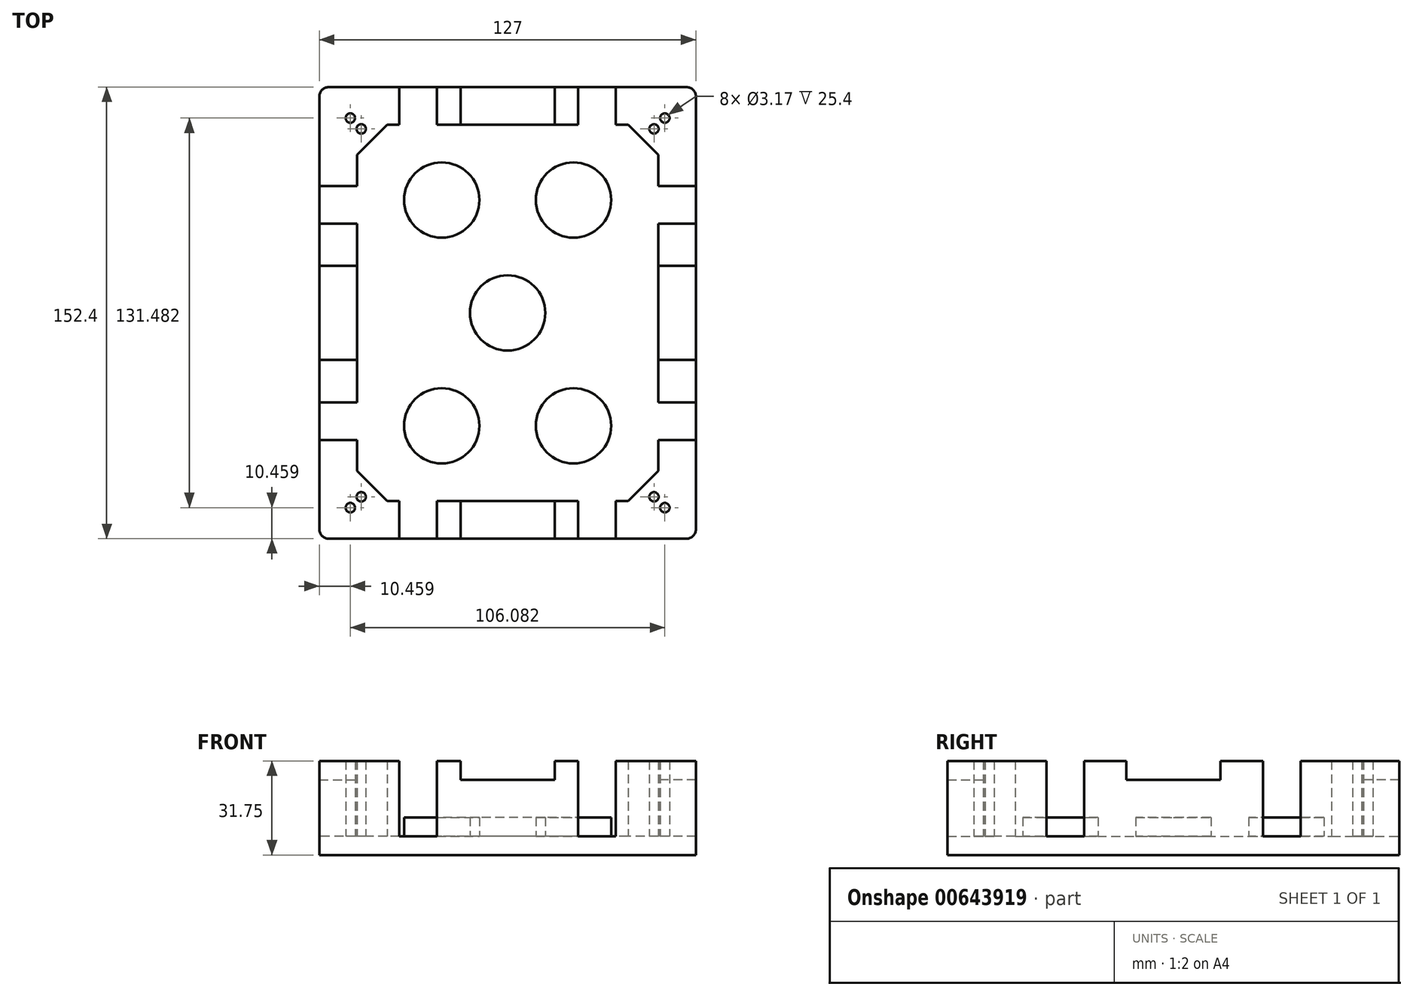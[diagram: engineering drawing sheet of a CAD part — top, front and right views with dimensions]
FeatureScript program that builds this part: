
annotation { "Feature Type Name" : "Feature", "Feature Type Description" : "" }
export const myFeature = defineFeature(function(context is Context, id is Id, definition is map)
    precondition{}
    {
        {
            var Q0;
            Q0=qCreatedBy(makeId("Top.planeOp"),FACE);
            var sketch = newSketch(context, id + "F0", { "sketchPlane" : qUnion([Q0])});
            skLineSegment(sketch, "E0.bottom", {"start": v(-60.32, 76.2) * mm, "end": v(60.33, 76.2) * mm});
            skLineSegment(sketch, "E0.top", {"start": v(-60.33, -76.2) * mm, "end": v(60.33, -76.2) * mm});
            skLineSegment(sketch, "E0.left", {"start": v(-63.5, 73.03) * mm, "end": v(-63.5, -73.03) * mm});
            skLineSegment(sketch, "E0.right", {"start": v(63.5, 73.03) * mm, "end": v(63.5, -73.03) * mm});
            skPoint(sketch, "E0.middle", {"position": v(0, 0) * mm});
            skLineSegment(sketch, "E1.bottom", {"start": v(-53.98, 69.85) * mm, "end": v(53.98, 69.85) * mm});
            skLineSegment(sketch, "E1.top", {"start": v(-53.98, -69.85) * mm, "end": v(53.97, -69.85) * mm});
            skLineSegment(sketch, "E1.left", {"start": v(-57.15, 66.68) * mm, "end": v(-57.15, -66.68) * mm});
            skLineSegment(sketch, "E1.right", {"start": v(57.15, 66.68) * mm, "end": v(57.15, -66.68) * mm});
            skLineSegment(sketch, "E2.bottom", {"start": v(-47.63, 63.5) * mm, "end": v(47.63, 63.5) * mm});
            skLineSegment(sketch, "E2.top", {"start": v(-47.63, -63.5) * mm, "end": v(48.25, -63.5) * mm});
            skLineSegment(sketch, "E2.left", {"start": v(-50.8, 60.33) * mm, "end": v(-50.8, -60.33) * mm});
            skLineSegment(sketch, "E2.right", {"start": v(50.8, 60.33) * mm, "end": v(50.8, -60.95) * mm});
            skPoint(sketch, "E3.visualSharp", {"position": v(-57.15, 69.85) * mm});
            skArc(sketch, "E3.filletArc", {"start": v(-53.98, 69.85) * mm, "mid": v(-56.22, 68.92) * mm, "end": v(-57.15, 66.68) * mm});
            skPoint(sketch, "E4.visualSharp", {"position": v(57.15, 69.85) * mm});
            skArc(sketch, "E4.filletArc", {"start": v(57.15, 66.68) * mm, "mid": v(56.22, 68.92) * mm, "end": v(53.98, 69.85) * mm});
            skPoint(sketch, "E5.visualSharp", {"position": v(57.15, -69.85) * mm});
            skArc(sketch, "E5.filletArc", {"start": v(53.97, -69.85) * mm, "mid": v(56.22, -68.92) * mm, "end": v(57.15, -66.68) * mm});
            skPoint(sketch, "E6.visualSharp", {"position": v(-57.15, -69.85) * mm});
            skArc(sketch, "E6.filletArc", {"start": v(-57.15, -66.68) * mm, "mid": v(-56.22, -68.92) * mm, "end": v(-53.98, -69.85) * mm});
            skPoint(sketch, "E7.visualSharp", {"position": v(50.8, 63.5) * mm});
            skArc(sketch, "E7.filletArc", {"start": v(50.8, 60.33) * mm, "mid": v(49.87, 62.57) * mm, "end": v(47.63, 63.5) * mm});
            skPoint(sketch, "E8.visualSharp", {"position": v(50.8, -63.5) * mm});
            skArc(sketch, "E8.filletArc", {"start": v(48.25, -63.5) * mm, "mid": v(50.05, -62.75) * mm, "end": v(50.8, -60.95) * mm});
            skPoint(sketch, "E9.visualSharp", {"position": v(-50.8, -63.5) * mm});
            skArc(sketch, "E9.filletArc", {"start": v(-50.8, -60.33) * mm, "mid": v(-49.87, -62.57) * mm, "end": v(-47.63, -63.5) * mm});
            skArc(sketch, "E10.filletArc", {"start": v(-47.63, 63.5) * mm, "mid": v(-49.87, 62.57) * mm, "end": v(-50.8, 60.33) * mm});
            skPoint(sketch, "E11.visualSharp", {"position": v(-63.5, 76.2) * mm});
            skArc(sketch, "E11.filletArc", {"start": v(-60.32, 76.2) * mm, "mid": v(-62.57, 75.27) * mm, "end": v(-63.5, 73.03) * mm});
            skPoint(sketch, "E12.visualSharp", {"position": v(63.5, 76.2) * mm});
            skArc(sketch, "E12.filletArc", {"start": v(63.5, 73.03) * mm, "mid": v(62.57, 75.27) * mm, "end": v(60.33, 76.2) * mm});
            skPoint(sketch, "E13.visualSharp", {"position": v(63.5, -76.2) * mm});
            skArc(sketch, "E13.filletArc", {"start": v(60.33, -76.2) * mm, "mid": v(62.57, -75.27) * mm, "end": v(63.5, -73.03) * mm});
            skPoint(sketch, "E14.visualSharp", {"position": v(-63.5, -76.2) * mm});
            skArc(sketch, "E14.filletArc", {"start": v(-63.5, -73.03) * mm, "mid": v(-62.57, -75.27) * mm, "end": v(-60.33, -76.2) * mm});
            skLineSegment(sketch, "E15.bottom", {"start": v(-34.92, 50.8) * mm, "end": v(34.93, 50.8) * mm});
            skLineSegment(sketch, "E15.top", {"start": v(-34.93, -50.8) * mm, "end": v(34.92, -50.8) * mm});
            skLineSegment(sketch, "E15.left", {"start": v(-34.92, 50.8) * mm, "end": v(-34.93, -50.8) * mm});
            skLineSegment(sketch, "E15.right", {"start": v(34.93, 50.8) * mm, "end": v(34.92, -50.8) * mm});
            skPoint(sketch, "E16", {"position": v(22.23, -50.8) * mm});
            skPoint(sketch, "E17", {"position": v(22.23, 50.8) * mm});
            skPoint(sketch, "E18", {"position": v(-22.22, 50.8) * mm});
            skPoint(sketch, "E19", {"position": v(-22.22, -50.8) * mm});
            skPoint(sketch, "E20", {"position": v(34.93, 38.1) * mm});
            skPoint(sketch, "E21", {"position": v(-34.92, 38.1) * mm});
            skPoint(sketch, "E22", {"position": v(34.92, -38.1) * mm});
            skPoint(sketch, "E23", {"position": v(-34.93, -38.1) * mm});
            skPoint(sketch, "E24", {"position": v(-22.22, 38.1) * mm});
            skPoint(sketch, "E25", {"position": v(22.23, 38.1) * mm});
            skPoint(sketch, "E26", {"position": v(22.23, -38.1) * mm});
            skPoint(sketch, "E27", {"position": v(-22.22, -38.1) * mm});
            skCircle(sketch, "E28", {"center": v(-22.22, 38.1) * mm, "radius": 12.7 * mm});
            skCircle(sketch, "E29", {"center": v(0, 0) * mm, "radius": 12.7 * mm});
            skCircle(sketch, "E30", {"center": v(22.23, 38.1) * mm, "radius": 12.7 * mm});
            skCircle(sketch, "E31", {"center": v(-22.22, -38.1) * mm, "radius": 12.7 * mm});
            skCircle(sketch, "E32", {"center": v(22.23, -38.1) * mm, "radius": 12.7 * mm});
            skPoint(sketch, "E33", {"position": v(15.88, 63.5) * mm});
            skPoint(sketch, "E34", {"position": v(15.88, 76.2) * mm});
            skPoint(sketch, "E35", {"position": v(15.88, -63.5) * mm});
            skPoint(sketch, "E36", {"position": v(15.88, -76.2) * mm});
            skPoint(sketch, "E37", {"position": v(-15.88, 76.2) * mm});
            skPoint(sketch, "E38", {"position": v(-15.88, 63.5) * mm});
            skPoint(sketch, "E39", {"position": v(-15.88, -63.5) * mm});
            skPoint(sketch, "E40", {"position": v(-15.88, -76.2) * mm});
            skPoint(sketch, "E41", {"position": v(0, 76.2) * mm});
            skPoint(sketch, "E42", {"position": v(0, -76.2) * mm});
            skPoint(sketch, "E43", {"position": v(-63.5, 0) * mm});
            skPoint(sketch, "E44", {"position": v(63.5, 0) * mm});
            skPoint(sketch, "E45", {"position": v(63.5, 15.88) * mm});
            skPoint(sketch, "E46", {"position": v(50.8, 15.88) * mm});
            skPoint(sketch, "E47", {"position": v(-50.8, 15.88) * mm});
            skPoint(sketch, "E48", {"position": v(-63.5, 15.88) * mm});
            skPoint(sketch, "E49", {"position": v(63.5, -15.88) * mm});
            skPoint(sketch, "E50", {"position": v(50.8, -15.88) * mm});
            skPoint(sketch, "E51", {"position": v(-50.8, -15.88) * mm});
            skPoint(sketch, "E52", {"position": v(-63.5, -15.88) * mm});
            skLineSegment(sketch, "E53", {"start": v(-15.88, 76.2) * mm, "end": v(-15.88, 63.5) * mm});
            skLineSegment(sketch, "E54", {"start": v(15.88, 76.2) * mm, "end": v(15.88, 63.5) * mm});
            skLineSegment(sketch, "E55", {"start": v(63.5, 15.88) * mm, "end": v(50.8, 15.88) * mm});
            skLineSegment(sketch, "E56", {"start": v(63.5, -15.88) * mm, "end": v(50.8, -15.88) * mm});
            skLineSegment(sketch, "E57", {"start": v(15.88, -76.2) * mm, "end": v(15.88, -63.5) * mm});
            skLineSegment(sketch, "E58", {"start": v(-15.88, -76.2) * mm, "end": v(-15.88, -63.5) * mm});
            skLineSegment(sketch, "E59", {"start": v(-63.5, -15.88) * mm, "end": v(-50.8, -15.88) * mm});
            skLineSegment(sketch, "E60", {"start": v(-63.5, 15.88) * mm, "end": v(-50.8, 15.88) * mm});
            skPoint(sketch, "E61", {"position": v(40.64, 63.5) * mm});
            skPoint(sketch, "E62", {"position": v(40.64, -63.5) * mm});
            skPoint(sketch, "E63", {"position": v(-40.64, 63.5) * mm});
            skPoint(sketch, "E64", {"position": v(-40.64, -63.5) * mm});
            skPoint(sketch, "E65", {"position": v(-50.8, -53.34) * mm});
            skPoint(sketch, "E66", {"position": v(50.8, -53.34) * mm});
            skPoint(sketch, "E67", {"position": v(50.8, 53.34) * mm});
            skPoint(sketch, "E68", {"position": v(-50.8, 53.34) * mm});
            skLineSegment(sketch, "E69", {"start": v(-50.8, 53.34) * mm, "end": v(-40.64, 63.5) * mm});
            skLineSegment(sketch, "E70", {"start": v(40.64, 63.5) * mm, "end": v(50.8, 53.34) * mm});
            skLineSegment(sketch, "E71", {"start": v(50.8, -53.34) * mm, "end": v(40.64, -63.5) * mm});
            skLineSegment(sketch, "E72", {"start": v(-40.64, -63.5) * mm, "end": v(-50.8, -53.34) * mm});
            skPoint(sketch, "E73", {"position": v(-45.72, 58.42) * mm});
            skPoint(sketch, "E74", {"position": v(45.72, 58.42) * mm});
            skPoint(sketch, "E75", {"position": v(45.72, -58.42) * mm});
            skPoint(sketch, "E76", {"position": v(-45.72, -58.42) * mm});
            skPoint(sketch, "E77", {"position": v(30.16, 76.2) * mm});
            skPoint(sketch, "E78", {"position": v(30.16, 63.5) * mm});
            skPoint(sketch, "E79", {"position": v(30.16, -63.5) * mm});
            skPoint(sketch, "E80", {"position": v(30.16, -76.2) * mm});
            skPoint(sketch, "E81", {"position": v(-30.16, 76.2) * mm});
            skPoint(sketch, "E82", {"position": v(-30.16, 63.5) * mm});
            skPoint(sketch, "E83", {"position": v(-30.16, -63.5) * mm});
            skPoint(sketch, "E84", {"position": v(-30.16, -76.2) * mm});
            skPoint(sketch, "E85", {"position": v(63.5, 36.51) * mm});
            skPoint(sketch, "E86", {"position": v(50.8, 36.51) * mm});
            skPoint(sketch, "E87", {"position": v(-50.8, 36.51) * mm});
            skPoint(sketch, "E88", {"position": v(-63.5, 36.51) * mm});
            skPoint(sketch, "E89", {"position": v(63.5, -36.51) * mm});
            skPoint(sketch, "E90", {"position": v(50.8, -36.51) * mm});
            skPoint(sketch, "E91", {"position": v(-50.8, -36.51) * mm});
            skPoint(sketch, "E92", {"position": v(-63.5, -36.51) * mm});
            skPoint(sketch, "E93", {"position": v(-36.51, 76.2) * mm});
            skPoint(sketch, "E94", {"position": v(-36.51, 63.5) * mm});
            skPoint(sketch, "E95", {"position": v(-36.51, -63.5) * mm});
            skPoint(sketch, "E96", {"position": v(-36.51, -76.2) * mm});
            skPoint(sketch, "E97", {"position": v(36.51, 76.2) * mm});
            skPoint(sketch, "E98", {"position": v(36.51, 63.5) * mm});
            skPoint(sketch, "E99", {"position": v(36.51, -63.5) * mm});
            skPoint(sketch, "E100", {"position": v(36.51, -76.2) * mm});
            skPoint(sketch, "E101", {"position": v(-23.81, 76.2) * mm});
            skPoint(sketch, "E102", {"position": v(-23.81, 63.5) * mm});
            skPoint(sketch, "E103", {"position": v(23.81, 76.2) * mm});
            skPoint(sketch, "E104", {"position": v(23.81, 63.5) * mm});
            skPoint(sketch, "E105", {"position": v(23.81, -63.5) * mm});
            skPoint(sketch, "E106", {"position": v(23.81, -76.2) * mm});
            skPoint(sketch, "E107", {"position": v(-23.81, -63.5) * mm});
            skPoint(sketch, "E108", {"position": v(-23.81, -76.2) * mm});
            skLineSegment(sketch, "E109", {"start": v(-36.51, 76.2) * mm, "end": v(-36.51, 63.5) * mm});
            skLineSegment(sketch, "E110", {"start": v(-23.81, 76.2) * mm, "end": v(-23.81, 63.5) * mm});
            skLineSegment(sketch, "E111", {"start": v(23.81, 76.2) * mm, "end": v(23.81, 63.5) * mm});
            skLineSegment(sketch, "E112", {"start": v(36.51, 76.2) * mm, "end": v(36.51, 63.5) * mm});
            skLineSegment(sketch, "E113", {"start": v(36.51, -63.5) * mm, "end": v(36.51, -76.2) * mm});
            skLineSegment(sketch, "E114", {"start": v(23.81, -63.5) * mm, "end": v(23.81, -76.2) * mm});
            skLineSegment(sketch, "E115", {"start": v(-23.81, -63.5) * mm, "end": v(-23.81, -76.2) * mm});
            skLineSegment(sketch, "E116", {"start": v(-36.51, -63.5) * mm, "end": v(-36.51, -76.2) * mm});
            skPoint(sketch, "E117", {"position": v(-63.5, 42.86) * mm});
            skPoint(sketch, "E118", {"position": v(-50.8, 42.86) * mm});
            skPoint(sketch, "E119", {"position": v(50.8, 42.86) * mm});
            skPoint(sketch, "E120", {"position": v(63.5, 42.86) * mm});
            skPoint(sketch, "E121", {"position": v(-63.5, 30.16) * mm});
            skPoint(sketch, "E122", {"position": v(-50.8, 30.16) * mm});
            skPoint(sketch, "E123", {"position": v(50.8, 30.16) * mm});
            skPoint(sketch, "E124", {"position": v(63.5, 30.16) * mm});
            skPoint(sketch, "E125", {"position": v(-63.5, -30.16) * mm});
            skPoint(sketch, "E126", {"position": v(-50.8, -30.16) * mm});
            skPoint(sketch, "E127", {"position": v(50.8, -30.16) * mm});
            skPoint(sketch, "E128", {"position": v(63.5, -30.16) * mm});
            skPoint(sketch, "E129", {"position": v(-63.5, -42.86) * mm});
            skPoint(sketch, "E130", {"position": v(-50.8, -42.86) * mm});
            skPoint(sketch, "E131", {"position": v(50.8, -42.86) * mm});
            skPoint(sketch, "E132", {"position": v(63.5, -42.86) * mm});
            skLineSegment(sketch, "E133", {"start": v(-63.5, 42.86) * mm, "end": v(-50.8, 42.86) * mm});
            skLineSegment(sketch, "E134", {"start": v(-63.5, 30.16) * mm, "end": v(-50.8, 30.16) * mm});
            skLineSegment(sketch, "E135", {"start": v(50.8, 42.86) * mm, "end": v(63.5, 42.86) * mm});
            skLineSegment(sketch, "E136", {"start": v(50.8, 30.16) * mm, "end": v(63.5, 30.16) * mm});
            skLineSegment(sketch, "E137", {"start": v(50.8, -30.16) * mm, "end": v(63.5, -30.16) * mm});
            skLineSegment(sketch, "E138", {"start": v(50.8, -42.86) * mm, "end": v(63.5, -42.86) * mm});
            skLineSegment(sketch, "E139", {"start": v(-50.8, -42.86) * mm, "end": v(-63.5, -42.86) * mm});
            skLineSegment(sketch, "E140", {"start": v(-50.8, -30.16) * mm, "end": v(-63.5, -30.16) * mm});
            skLineSegment(sketch, "E141", {"start": v(57.15, 69.85) * mm, "end": v(45.72, 58.42) * mm, "construction": true});
            skLineSegment(sketch, "E142", {"start": v(57.15, -69.85) * mm, "end": v(45.72, -58.42) * mm, "construction": true});
            skLineSegment(sketch, "E143", {"start": v(-57.15, -69.85) * mm, "end": v(-45.72, -58.42) * mm, "construction": true});
            skPoint(sketch, "E144", {"position": v(53.04, 65.74) * mm});
            skLineSegment(sketch, "E145", {"start": v(-57.15, 69.85) * mm, "end": v(-45.72, 58.42) * mm, "construction": true});
            skPoint(sketch, "E146", {"position": v(-53.04, 65.74) * mm});
            skPoint(sketch, "E147", {"position": v(53.04, -65.74) * mm});
            skPoint(sketch, "E148", {"position": v(-53.04, -65.74) * mm});
            skCircle(sketch, "E149", {"center": v(-53.04, 65.74) * mm, "radius": 1.59 * mm});
            skCircle(sketch, "E150", {"center": v(53.04, 65.74) * mm, "radius": 1.59 * mm});
            skCircle(sketch, "E151", {"center": v(53.04, -65.74) * mm, "radius": 1.59 * mm});
            skCircle(sketch, "E152", {"center": v(-53.04, -65.74) * mm, "radius": 1.59 * mm});
            skPoint(sketch, "E153", {"position": v(-49.38, -62.08) * mm});
            skPoint(sketch, "E154", {"position": v(49.38, -62.08) * mm});
            skCircle(sketch, "E155", {"center": v(-49.38, -62.08) * mm, "radius": 1.59 * mm});
            skCircle(sketch, "E156", {"center": v(49.38, -62.08) * mm, "radius": 1.59 * mm});
            skPoint(sketch, "E157", {"position": v(-49.38, 62.08) * mm});
            skPoint(sketch, "E158", {"position": v(49.38, 62.08) * mm});
            skCircle(sketch, "E159", {"center": v(-49.38, 62.08) * mm, "radius": 1.59 * mm});
            skCircle(sketch, "E160", {"center": v(49.38, 62.08) * mm, "radius": 1.59 * mm});
            skSolve(sketch);
        }
        {
            var Q0;
            {var subQ0=sQuery(id+"F0.wireOp",EDGE,"E30");var subQ1=makeQuery(id+"F0.imprint","INTERSECT",VERTEX,{"derivedFrom":[sQuery(id+"F0.wireOp",EDGE,"E15.bottom"),subQ0]});Q0=makeQuery(id+"F0.imprint","IMPRINT",FACE,{"disambiguationData":[TD([[makeQuery(id+"F0.imprint","IMPRINT",EDGE,{"disambiguationData":[TD([[subQ1,1.0]])],"derivedFrom":subQ0}),1.0]])]});}
            var Q1;
            {var subQ0=sQuery(id+"F0.wireOp",EDGE,"E15.right");var subQ1=sQuery(id+"F0.wireOp",EDGE,"E15.bottom");var subQ2=makeQuery(id+"F0.imprint","INTERSECT",VERTEX,{"derivedFrom":[subQ1,subQ0]});Q1=makeQuery(id+"F0.imprint","IMPRINT",FACE,{"disambiguationData":[TD([[makeQuery(id+"F0.imprint","IMPRINT",EDGE,{"disambiguationData":[TD([[subQ2,1.0]])],"derivedFrom":subQ1}),-1.0]])]});}
            var Q2;
            {var subQ5=sQuery(id+"F0.wireOp",EDGE,"E6.filletArc");Q2=makeQuery(id+"F0.imprint","IMPRINT",FACE,{"disambiguationData":[TD([[makeQuery(id+"F0.imprint","IMPRINT",EDGE,{"derivedFrom":subQ5}),1.0]])]});}
            var Q3;
            {var subQ0=sQuery(id+"F0.wireOp",EDGE,"E15.right");var subQ1=sQuery(id+"F0.wireOp",EDGE,"E15.top");var subQ2=makeQuery(id+"F0.imprint","INTERSECT",VERTEX,{"derivedFrom":[subQ1,subQ0]});Q3=makeQuery(id+"F0.imprint","IMPRINT",FACE,{"disambiguationData":[TD([[makeQuery(id+"F0.imprint","IMPRINT",EDGE,{"disambiguationData":[TD([[subQ2,1.0]])],"derivedFrom":subQ1}),1.0]])]});}
            var Q4;
            Q4=makeQuery(id+"F0.imprint","IMPRINT",FACE,{"disambiguationData":[TD([[makeQuery(id+"F0.imprint","IMPRINT",EDGE,{"derivedFrom":sQuery(id+"F0.wireOp",EDGE,"E29")}),-1.0]])]});
            var Q5;
            {var subQ0=sQuery(id+"F0.wireOp",EDGE,"E10.filletArc");Q5=makeQuery(id+"F0.imprint","IMPRINT",FACE,{"disambiguationData":[TD([[makeQuery(id+"F0.imprint","IMPRINT",EDGE,{"derivedFrom":subQ0}),1.0]])]});}
            var Q6;
            {var subQ0=sQuery(id+"F0.wireOp",EDGE,"E139");var subQ1=sQuery(id+"F0.wireOp",EDGE,"E0.left");var subQ2=makeQuery(id+"F0.imprint","INTERSECT",VERTEX,{"derivedFrom":[subQ1,subQ0]});Q6=makeQuery(id+"F0.imprint","IMPRINT",FACE,{"disambiguationData":[TD([[makeQuery(id+"F0.imprint","IMPRINT",EDGE,{"disambiguationData":[TD([[subQ2,1.0]])],"derivedFrom":subQ1}),1.0]])]});}
            var Q7;
            {var subQ0=sQuery(id+"F0.wireOp",EDGE,"E6.filletArc");Q7=makeQuery(id+"F0.imprint","IMPRINT",FACE,{"disambiguationData":[TD([[makeQuery(id+"F0.imprint","IMPRINT",EDGE,{"derivedFrom":subQ0}),-1.0]])]});}
            var Q8;
            {var subQ0=sQuery(id+"F0.wireOp",EDGE,"E56");var subQ1=sQuery(id+"F0.wireOp",EDGE,"E0.right");var subQ2=makeQuery(id+"F0.imprint","INTERSECT",VERTEX,{"derivedFrom":[subQ1,subQ0]});Q8=makeQuery(id+"F0.imprint","IMPRINT",FACE,{"disambiguationData":[TD([[makeQuery(id+"F0.imprint","IMPRINT",EDGE,{"disambiguationData":[TD([[subQ2,-1.0]])],"derivedFrom":subQ1}),-1.0]])]});}
            var Q9;
            {var subQ0=sQuery(id+"F0.wireOp",EDGE,"E57");var subQ1=sQuery(id+"F0.wireOp",EDGE,"E1.top");var subQ2=makeQuery(id+"F0.imprint","INTERSECT",VERTEX,{"derivedFrom":[subQ1,subQ0]});Q9=makeQuery(id+"F0.imprint","IMPRINT",FACE,{"disambiguationData":[TD([[makeQuery(id+"F0.imprint","IMPRINT",EDGE,{"disambiguationData":[TD([[subQ2,-1.0]])],"derivedFrom":subQ1}),1.0]])]});}
            var Q10;
            {var subQ0=sQuery(id+"F0.wireOp",EDGE,"E59");var subQ1=sQuery(id+"F0.wireOp",EDGE,"E0.left");var subQ2=makeQuery(id+"F0.imprint","INTERSECT",VERTEX,{"derivedFrom":[subQ1,subQ0]});Q10=makeQuery(id+"F0.imprint","IMPRINT",FACE,{"disambiguationData":[TD([[makeQuery(id+"F0.imprint","IMPRINT",EDGE,{"disambiguationData":[TD([[subQ2,1.0]])],"derivedFrom":subQ1}),1.0]])]});}
            var Q11;
            {var subQ0=sQuery(id+"F0.wireOp",EDGE,"E135");var subQ1=sQuery(id+"F0.wireOp",EDGE,"E1.right");var subQ2=makeQuery(id+"F0.imprint","INTERSECT",VERTEX,{"derivedFrom":[subQ1,subQ0]});Q11=makeQuery(id+"F0.imprint","IMPRINT",FACE,{"disambiguationData":[TD([[makeQuery(id+"F0.imprint","IMPRINT",EDGE,{"disambiguationData":[TD([[subQ2,-1.0]])],"derivedFrom":subQ1}),-1.0]])]});}
            var Q12;
            {var subQ0=sQuery(id+"F0.wireOp",EDGE,"E111");var subQ1=sQuery(id+"F0.wireOp",EDGE,"E0.bottom");var subQ2=makeQuery(id+"F0.imprint","INTERSECT",VERTEX,{"derivedFrom":[subQ1,subQ0]});Q12=makeQuery(id+"F0.imprint","IMPRINT",FACE,{"disambiguationData":[TD([[makeQuery(id+"F0.imprint","IMPRINT",EDGE,{"disambiguationData":[TD([[subQ2,-1.0]])],"derivedFrom":subQ1}),-1.0]])]});}
            var Q13;
            Q13=makeQuery(id+"F0.imprint","IMPRINT",FACE,{"disambiguationData":[TD([[makeQuery(id+"F0.imprint","IMPRINT",EDGE,{"derivedFrom":sQuery(id+"F0.wireOp",EDGE,"E29")}),1.0]])]});
            var Q14;
            {var subQ0=sQuery(id+"F0.wireOp",EDGE,"E137");var subQ1=sQuery(id+"F0.wireOp",EDGE,"E0.right");var subQ2=makeQuery(id+"F0.imprint","INTERSECT",VERTEX,{"derivedFrom":[subQ1,subQ0]});Q14=makeQuery(id+"F0.imprint","IMPRINT",FACE,{"disambiguationData":[TD([[makeQuery(id+"F0.imprint","IMPRINT",EDGE,{"disambiguationData":[TD([[subQ2,-1.0]])],"derivedFrom":subQ1}),-1.0]])]});}
            var Q15;
            {var subQ0=sQuery(id+"F0.wireOp",EDGE,"E31");var subQ1=makeQuery(id+"F0.imprint","INTERSECT",VERTEX,{"derivedFrom":[sQuery(id+"F0.wireOp",EDGE,"E15.top"),subQ0]});Q15=makeQuery(id+"F0.imprint","IMPRINT",FACE,{"disambiguationData":[TD([[makeQuery(id+"F0.imprint","IMPRINT",EDGE,{"disambiguationData":[TD([[subQ1,1.0]])],"derivedFrom":subQ0}),1.0]])]});}
            var Q16;
            {var subQ0=sQuery(id+"F0.wireOp",EDGE,"E59");var subQ1=sQuery(id+"F0.wireOp",EDGE,"E1.left");var subQ2=makeQuery(id+"F0.imprint","INTERSECT",VERTEX,{"derivedFrom":[subQ1,subQ0]});Q16=makeQuery(id+"F0.imprint","IMPRINT",FACE,{"disambiguationData":[TD([[makeQuery(id+"F0.imprint","IMPRINT",EDGE,{"disambiguationData":[TD([[subQ2,-1.0]])],"derivedFrom":subQ1}),1.0]])]});}
            var Q17;
            {var subQ0=sQuery(id+"F0.wireOp",EDGE,"E9.filletArc");Q17=makeQuery(id+"F0.imprint","IMPRINT",FACE,{"disambiguationData":[TD([[makeQuery(id+"F0.imprint","IMPRINT",EDGE,{"derivedFrom":subQ0}),1.0]])]});}
            var Q18;
            {var subQ0=sQuery(id+"F0.wireOp",EDGE,"E32");var subQ1=makeQuery(id+"F0.imprint","INTERSECT",VERTEX,{"derivedFrom":[sQuery(id+"F0.wireOp",EDGE,"E15.top"),subQ0]});Q18=makeQuery(id+"F0.imprint","IMPRINT",FACE,{"disambiguationData":[TD([[makeQuery(id+"F0.imprint","IMPRINT",EDGE,{"disambiguationData":[TD([[subQ1,1.0]])],"derivedFrom":subQ0}),1.0]])]});}
            var Q19;
            {var subQ0=sQuery(id+"F0.wireOp",EDGE,"E115");var subQ1=sQuery(id+"F0.wireOp",EDGE,"E1.top");var subQ2=makeQuery(id+"F0.imprint","INTERSECT",VERTEX,{"derivedFrom":[subQ1,subQ0]});Q19=makeQuery(id+"F0.imprint","IMPRINT",FACE,{"disambiguationData":[TD([[makeQuery(id+"F0.imprint","IMPRINT",EDGE,{"disambiguationData":[TD([[subQ2,-1.0]])],"derivedFrom":subQ1}),1.0]])]});}
            var Q20;
            {var subQ0=sQuery(id+"F0.wireOp",EDGE,"E135");var subQ1=sQuery(id+"F0.wireOp",EDGE,"E0.right");var subQ2=makeQuery(id+"F0.imprint","INTERSECT",VERTEX,{"derivedFrom":[subQ1,subQ0]});Q20=makeQuery(id+"F0.imprint","IMPRINT",FACE,{"disambiguationData":[TD([[makeQuery(id+"F0.imprint","IMPRINT",EDGE,{"disambiguationData":[TD([[subQ2,-1.0]])],"derivedFrom":subQ1}),-1.0]])]});}
            var Q21;
            {var subQ0=sQuery(id+"F0.wireOp",EDGE,"E57");var subQ1=sQuery(id+"F0.wireOp",EDGE,"E0.top");var subQ2=makeQuery(id+"F0.imprint","INTERSECT",VERTEX,{"derivedFrom":[subQ1,subQ0]});Q21=makeQuery(id+"F0.imprint","IMPRINT",FACE,{"disambiguationData":[TD([[makeQuery(id+"F0.imprint","IMPRINT",EDGE,{"disambiguationData":[TD([[subQ2,1.0]])],"derivedFrom":subQ1}),1.0]])]});}
            var Q22;
            {var subQ0=sQuery(id+"F0.wireOp",EDGE,"E134");var subQ1=sQuery(id+"F0.wireOp",EDGE,"E1.left");var subQ2=makeQuery(id+"F0.imprint","INTERSECT",VERTEX,{"derivedFrom":[subQ1,subQ0]});Q22=makeQuery(id+"F0.imprint","IMPRINT",FACE,{"disambiguationData":[TD([[makeQuery(id+"F0.imprint","IMPRINT",EDGE,{"disambiguationData":[TD([[subQ2,-1.0]])],"derivedFrom":subQ1}),1.0]])]});}
            var Q23;
            {var subQ8=sQuery(id+"F0.wireOp",EDGE,"E4.filletArc");Q23=makeQuery(id+"F0.imprint","IMPRINT",FACE,{"disambiguationData":[TD([[makeQuery(id+"F0.imprint","IMPRINT",EDGE,{"derivedFrom":subQ8}),1.0]])]});}
            var Q24;
            {var subQ0=sQuery(id+"F0.wireOp",EDGE,"E7.filletArc");Q24=makeQuery(id+"F0.imprint","IMPRINT",FACE,{"disambiguationData":[TD([[makeQuery(id+"F0.imprint","IMPRINT",EDGE,{"derivedFrom":subQ0}),1.0]])]});}
            var Q25;
            {var subQ0=sQuery(id+"F0.wireOp",EDGE,"E133");var subQ1=sQuery(id+"F0.wireOp",EDGE,"E0.left");var subQ2=makeQuery(id+"F0.imprint","INTERSECT",VERTEX,{"derivedFrom":[subQ1,subQ0]});Q25=makeQuery(id+"F0.imprint","IMPRINT",FACE,{"disambiguationData":[TD([[makeQuery(id+"F0.imprint","IMPRINT",EDGE,{"disambiguationData":[TD([[subQ2,-1.0]])],"derivedFrom":subQ1}),1.0]])]});}
            var Q26;
            {var subQ0=sQuery(id+"F0.wireOp",EDGE,"E54");var subQ1=sQuery(id+"F0.wireOp",EDGE,"E0.bottom");var subQ2=makeQuery(id+"F0.imprint","INTERSECT",VERTEX,{"derivedFrom":[subQ1,subQ0]});Q26=makeQuery(id+"F0.imprint","IMPRINT",FACE,{"disambiguationData":[TD([[makeQuery(id+"F0.imprint","IMPRINT",EDGE,{"disambiguationData":[TD([[subQ2,-1.0]])],"derivedFrom":subQ1}),-1.0]])]});}
            var Q27;
            {var subQ0=sQuery(id+"F0.wireOp",EDGE,"E53");var subQ1=sQuery(id+"F0.wireOp",EDGE,"E1.bottom");var subQ2=makeQuery(id+"F0.imprint","INTERSECT",VERTEX,{"derivedFrom":[subQ1,subQ0]});Q27=makeQuery(id+"F0.imprint","IMPRINT",FACE,{"disambiguationData":[TD([[makeQuery(id+"F0.imprint","IMPRINT",EDGE,{"disambiguationData":[TD([[subQ2,-1.0]])],"derivedFrom":subQ1}),-1.0]])]});}
            var Q28;
            {var subQ0=sQuery(id+"F0.wireOp",EDGE,"E53");var subQ1=sQuery(id+"F0.wireOp",EDGE,"E0.bottom");var subQ2=makeQuery(id+"F0.imprint","INTERSECT",VERTEX,{"derivedFrom":[subQ1,subQ0]});Q28=makeQuery(id+"F0.imprint","IMPRINT",FACE,{"disambiguationData":[TD([[makeQuery(id+"F0.imprint","IMPRINT",EDGE,{"disambiguationData":[TD([[subQ2,-1.0]])],"derivedFrom":subQ1}),-1.0]])]});}
            var Q29;
            {var subQ0=sQuery(id+"F0.wireOp",EDGE,"E115");var subQ1=sQuery(id+"F0.wireOp",EDGE,"E0.top");var subQ2=makeQuery(id+"F0.imprint","INTERSECT",VERTEX,{"derivedFrom":[subQ1,subQ0]});Q29=makeQuery(id+"F0.imprint","IMPRINT",FACE,{"disambiguationData":[TD([[makeQuery(id+"F0.imprint","IMPRINT",EDGE,{"disambiguationData":[TD([[subQ2,1.0]])],"derivedFrom":subQ1}),1.0]])]});}
            var Q30;
            {var subQ0=sQuery(id+"F0.wireOp",EDGE,"E56");var subQ1=sQuery(id+"F0.wireOp",EDGE,"E1.right");var subQ2=makeQuery(id+"F0.imprint","INTERSECT",VERTEX,{"derivedFrom":[subQ1,subQ0]});Q30=makeQuery(id+"F0.imprint","IMPRINT",FACE,{"disambiguationData":[TD([[makeQuery(id+"F0.imprint","IMPRINT",EDGE,{"disambiguationData":[TD([[subQ2,-1.0]])],"derivedFrom":subQ1}),-1.0]])]});}
            var Q31;
            {var subQ0=sQuery(id+"F0.wireOp",EDGE,"E3.filletArc");Q31=makeQuery(id+"F0.imprint","IMPRINT",FACE,{"disambiguationData":[TD([[makeQuery(id+"F0.imprint","IMPRINT",EDGE,{"derivedFrom":subQ0}),-1.0]])]});}
            var Q32;
            {var subQ6=sQuery(id+"F0.wireOp",EDGE,"E69");Q32=makeQuery(id+"F0.imprint","IMPRINT",FACE,{"disambiguationData":[TD([[makeQuery(id+"F0.imprint","IMPRINT",EDGE,{"derivedFrom":subQ6}),-1.0]])]});}
            var Q33;
            {var subQ0=sQuery(id+"F0.wireOp",EDGE,"E28");var subQ1=makeQuery(id+"F0.imprint","INTERSECT",VERTEX,{"derivedFrom":[sQuery(id+"F0.wireOp",EDGE,"E15.bottom"),subQ0]});Q33=makeQuery(id+"F0.imprint","IMPRINT",FACE,{"disambiguationData":[TD([[makeQuery(id+"F0.imprint","IMPRINT",EDGE,{"disambiguationData":[TD([[subQ1,-1.0]])],"derivedFrom":subQ0}),1.0]])]});}
            var Q34;
            {var subQ0=sQuery(id+"F0.wireOp",EDGE,"E114");var subQ1=sQuery(id+"F0.wireOp",EDGE,"E1.top");var subQ2=makeQuery(id+"F0.imprint","INTERSECT",VERTEX,{"derivedFrom":[subQ1,subQ0]});Q34=makeQuery(id+"F0.imprint","IMPRINT",FACE,{"disambiguationData":[TD([[makeQuery(id+"F0.imprint","IMPRINT",EDGE,{"disambiguationData":[TD([[subQ2,-1.0]])],"derivedFrom":subQ1}),1.0]])]});}
            var Q35;
            {var subQ0=sQuery(id+"F0.wireOp",EDGE,"E136");var subQ1=sQuery(id+"F0.wireOp",EDGE,"E1.right");var subQ2=makeQuery(id+"F0.imprint","INTERSECT",VERTEX,{"derivedFrom":[subQ1,subQ0]});Q35=makeQuery(id+"F0.imprint","IMPRINT",FACE,{"disambiguationData":[TD([[makeQuery(id+"F0.imprint","IMPRINT",EDGE,{"disambiguationData":[TD([[subQ2,-1.0]])],"derivedFrom":subQ1}),-1.0]])]});}
            var Q36;
            {var subQ0=sQuery(id+"F0.wireOp",EDGE,"E59");var subQ1=sQuery(id+"F0.wireOp",EDGE,"E0.left");var subQ2=makeQuery(id+"F0.imprint","INTERSECT",VERTEX,{"derivedFrom":[subQ1,subQ0]});Q36=makeQuery(id+"F0.imprint","IMPRINT",FACE,{"disambiguationData":[TD([[makeQuery(id+"F0.imprint","IMPRINT",EDGE,{"disambiguationData":[TD([[subQ2,-1.0]])],"derivedFrom":subQ1}),1.0]])]});}
            var Q37;
            {var subQ0=sQuery(id+"F0.wireOp",EDGE,"E53");var subQ1=sQuery(id+"F0.wireOp",EDGE,"E0.bottom");var subQ2=makeQuery(id+"F0.imprint","INTERSECT",VERTEX,{"derivedFrom":[subQ1,subQ0]});Q37=makeQuery(id+"F0.imprint","IMPRINT",FACE,{"disambiguationData":[TD([[makeQuery(id+"F0.imprint","IMPRINT",EDGE,{"disambiguationData":[TD([[subQ2,1.0]])],"derivedFrom":subQ1}),-1.0]])]});}
            var Q38;
            {var subQ0=sQuery(id+"F0.wireOp",EDGE,"E15.left");var subQ1=sQuery(id+"F0.wireOp",EDGE,"E15.top");var subQ2=makeQuery(id+"F0.imprint","INTERSECT",VERTEX,{"derivedFrom":[subQ1,subQ0]});Q38=makeQuery(id+"F0.imprint","IMPRINT",FACE,{"disambiguationData":[TD([[makeQuery(id+"F0.imprint","IMPRINT",EDGE,{"disambiguationData":[TD([[subQ2,-1.0]])],"derivedFrom":subQ1}),1.0]])]});}
            var Q39;
            {var subQ0=sQuery(id+"F0.wireOp",EDGE,"E60");var subQ1=sQuery(id+"F0.wireOp",EDGE,"E1.left");var subQ2=makeQuery(id+"F0.imprint","INTERSECT",VERTEX,{"derivedFrom":[subQ1,subQ0]});Q39=makeQuery(id+"F0.imprint","IMPRINT",FACE,{"disambiguationData":[TD([[makeQuery(id+"F0.imprint","IMPRINT",EDGE,{"disambiguationData":[TD([[subQ2,-1.0]])],"derivedFrom":subQ1}),1.0]])]});}
            var Q40;
            {var subQ0=sQuery(id+"F0.wireOp",EDGE,"E110");var subQ1=sQuery(id+"F0.wireOp",EDGE,"E1.bottom");var subQ2=makeQuery(id+"F0.imprint","INTERSECT",VERTEX,{"derivedFrom":[subQ1,subQ0]});Q40=makeQuery(id+"F0.imprint","IMPRINT",FACE,{"disambiguationData":[TD([[makeQuery(id+"F0.imprint","IMPRINT",EDGE,{"disambiguationData":[TD([[subQ2,-1.0]])],"derivedFrom":subQ1}),-1.0]])]});}
            var Q41;
            {var subQ0=sQuery(id+"F0.wireOp",EDGE,"E55");var subQ1=sQuery(id+"F0.wireOp",EDGE,"E0.right");var subQ2=makeQuery(id+"F0.imprint","INTERSECT",VERTEX,{"derivedFrom":[subQ1,subQ0]});Q41=makeQuery(id+"F0.imprint","IMPRINT",FACE,{"disambiguationData":[TD([[makeQuery(id+"F0.imprint","IMPRINT",EDGE,{"disambiguationData":[TD([[subQ2,1.0]])],"derivedFrom":subQ1}),-1.0]])]});}
            var Q42;
            {var subQ0=sQuery(id+"F0.wireOp",EDGE,"E58");var subQ1=sQuery(id+"F0.wireOp",EDGE,"E0.top");var subQ2=makeQuery(id+"F0.imprint","INTERSECT",VERTEX,{"derivedFrom":[subQ1,subQ0]});Q42=makeQuery(id+"F0.imprint","IMPRINT",FACE,{"disambiguationData":[TD([[makeQuery(id+"F0.imprint","IMPRINT",EDGE,{"disambiguationData":[TD([[subQ2,1.0]])],"derivedFrom":subQ1}),1.0]])]});}
            var Q43;
            {var subQ0=sQuery(id+"F0.wireOp",EDGE,"E15.left");var subQ1=sQuery(id+"F0.wireOp",EDGE,"E15.bottom");var subQ2=makeQuery(id+"F0.imprint","INTERSECT",VERTEX,{"derivedFrom":[subQ1,subQ0]});Q43=makeQuery(id+"F0.imprint","IMPRINT",FACE,{"disambiguationData":[TD([[makeQuery(id+"F0.imprint","IMPRINT",EDGE,{"disambiguationData":[TD([[subQ2,-1.0]])],"derivedFrom":subQ1}),-1.0]])]});}
            var Q44;
            {var subQ0=sQuery(id+"F0.wireOp",EDGE,"E113");var subQ1=sQuery(id+"F0.wireOp",EDGE,"E0.top");var subQ2=makeQuery(id+"F0.imprint","INTERSECT",VERTEX,{"derivedFrom":[subQ1,subQ0]});Q44=makeQuery(id+"F0.imprint","IMPRINT",FACE,{"disambiguationData":[TD([[makeQuery(id+"F0.imprint","IMPRINT",EDGE,{"disambiguationData":[TD([[subQ2,1.0]])],"derivedFrom":subQ1}),1.0]])]});}
            var Q45;
            {var subQ0=sQuery(id+"F0.wireOp",EDGE,"E8.filletArc");Q45=makeQuery(id+"F0.imprint","IMPRINT",FACE,{"disambiguationData":[TD([[makeQuery(id+"F0.imprint","IMPRINT",EDGE,{"derivedFrom":subQ0}),1.0]])]});}
            var Q46;
            {var subQ0=sQuery(id+"F0.wireOp",EDGE,"E55");var subQ1=sQuery(id+"F0.wireOp",EDGE,"E1.right");var subQ2=makeQuery(id+"F0.imprint","INTERSECT",VERTEX,{"derivedFrom":[subQ1,subQ0]});Q46=makeQuery(id+"F0.imprint","IMPRINT",FACE,{"disambiguationData":[TD([[makeQuery(id+"F0.imprint","IMPRINT",EDGE,{"disambiguationData":[TD([[subQ2,-1.0]])],"derivedFrom":subQ1}),-1.0]])]});}
            var Q47;
            {var subQ0=sQuery(id+"F0.wireOp",EDGE,"E109");var subQ1=sQuery(id+"F0.wireOp",EDGE,"E0.bottom");var subQ2=makeQuery(id+"F0.imprint","INTERSECT",VERTEX,{"derivedFrom":[subQ1,subQ0]});Q47=makeQuery(id+"F0.imprint","IMPRINT",FACE,{"disambiguationData":[TD([[makeQuery(id+"F0.imprint","IMPRINT",EDGE,{"disambiguationData":[TD([[subQ2,-1.0]])],"derivedFrom":subQ1}),-1.0]])]});}
            var Q48;
            {var subQ0=sQuery(id+"F0.wireOp",EDGE,"E57");var subQ1=sQuery(id+"F0.wireOp",EDGE,"E0.top");var subQ2=makeQuery(id+"F0.imprint","INTERSECT",VERTEX,{"derivedFrom":[subQ1,subQ0]});Q48=makeQuery(id+"F0.imprint","IMPRINT",FACE,{"disambiguationData":[TD([[makeQuery(id+"F0.imprint","IMPRINT",EDGE,{"disambiguationData":[TD([[subQ2,-1.0]])],"derivedFrom":subQ1}),1.0]])]});}
            var Q49;
            {var subQ6=sQuery(id+"F0.wireOp",EDGE,"E5.filletArc");Q49=makeQuery(id+"F0.imprint","IMPRINT",FACE,{"disambiguationData":[TD([[makeQuery(id+"F0.imprint","IMPRINT",EDGE,{"derivedFrom":subQ6}),1.0]])]});}
            var Q50;
            {var subQ0=sQuery(id+"F0.wireOp",EDGE,"E58");var subQ1=sQuery(id+"F0.wireOp",EDGE,"E1.top");var subQ2=makeQuery(id+"F0.imprint","INTERSECT",VERTEX,{"derivedFrom":[subQ1,subQ0]});Q50=makeQuery(id+"F0.imprint","IMPRINT",FACE,{"disambiguationData":[TD([[makeQuery(id+"F0.imprint","IMPRINT",EDGE,{"disambiguationData":[TD([[subQ2,-1.0]])],"derivedFrom":subQ1}),1.0]])]});}
            var Q51;
            {var subQ0=sQuery(id+"F0.wireOp",EDGE,"E60");var subQ1=sQuery(id+"F0.wireOp",EDGE,"E0.left");var subQ2=makeQuery(id+"F0.imprint","INTERSECT",VERTEX,{"derivedFrom":[subQ1,subQ0]});Q51=makeQuery(id+"F0.imprint","IMPRINT",FACE,{"disambiguationData":[TD([[makeQuery(id+"F0.imprint","IMPRINT",EDGE,{"disambiguationData":[TD([[subQ2,1.0]])],"derivedFrom":subQ1}),1.0]])]});}
            var Q52;
            {var subQ0=sQuery(id+"F0.wireOp",EDGE,"E116");var subQ1=sQuery(id+"F0.wireOp",EDGE,"E1.top");var subQ2=makeQuery(id+"F0.imprint","INTERSECT",VERTEX,{"derivedFrom":[subQ1,subQ0]});Q52=makeQuery(id+"F0.imprint","IMPRINT",FACE,{"disambiguationData":[TD([[makeQuery(id+"F0.imprint","IMPRINT",EDGE,{"disambiguationData":[TD([[subQ2,-1.0]])],"derivedFrom":subQ1}),1.0]])]});}
            var Q53;
            {var subQ0=sQuery(id+"F0.wireOp",EDGE,"E140");var subQ1=sQuery(id+"F0.wireOp",EDGE,"E1.left");var subQ2=makeQuery(id+"F0.imprint","INTERSECT",VERTEX,{"derivedFrom":[subQ1,subQ0]});Q53=makeQuery(id+"F0.imprint","IMPRINT",FACE,{"disambiguationData":[TD([[makeQuery(id+"F0.imprint","IMPRINT",EDGE,{"disambiguationData":[TD([[subQ2,-1.0]])],"derivedFrom":subQ1}),1.0]])]});}
            var Q54;
            {var subQ0=sQuery(id+"F0.wireOp",EDGE,"E4.filletArc");Q54=makeQuery(id+"F0.imprint","IMPRINT",FACE,{"disambiguationData":[TD([[makeQuery(id+"F0.imprint","IMPRINT",EDGE,{"derivedFrom":subQ0}),-1.0]])]});}
            var Q55;
            {var subQ0=sQuery(id+"F0.wireOp",EDGE,"E133");var subQ1=sQuery(id+"F0.wireOp",EDGE,"E1.left");var subQ2=makeQuery(id+"F0.imprint","INTERSECT",VERTEX,{"derivedFrom":[subQ1,subQ0]});Q55=makeQuery(id+"F0.imprint","IMPRINT",FACE,{"disambiguationData":[TD([[makeQuery(id+"F0.imprint","IMPRINT",EDGE,{"disambiguationData":[TD([[subQ2,-1.0]])],"derivedFrom":subQ1}),1.0]])]});}
            var Q56;
            {var subQ0=sQuery(id+"F0.wireOp",EDGE,"E5.filletArc");Q56=makeQuery(id+"F0.imprint","IMPRINT",FACE,{"disambiguationData":[TD([[makeQuery(id+"F0.imprint","IMPRINT",EDGE,{"derivedFrom":subQ0}),-1.0]])]});}
            var Q57;
            {var subQ0=sQuery(id+"F0.wireOp",EDGE,"E109");var subQ1=sQuery(id+"F0.wireOp",EDGE,"E1.bottom");var subQ2=makeQuery(id+"F0.imprint","INTERSECT",VERTEX,{"derivedFrom":[subQ1,subQ0]});Q57=makeQuery(id+"F0.imprint","IMPRINT",FACE,{"disambiguationData":[TD([[makeQuery(id+"F0.imprint","IMPRINT",EDGE,{"disambiguationData":[TD([[subQ2,-1.0]])],"derivedFrom":subQ1}),-1.0]])]});}
            var Q58;
            {var subQ0=sQuery(id+"F0.wireOp",EDGE,"E54");var subQ1=sQuery(id+"F0.wireOp",EDGE,"E1.bottom");var subQ2=makeQuery(id+"F0.imprint","INTERSECT",VERTEX,{"derivedFrom":[subQ1,subQ0]});Q58=makeQuery(id+"F0.imprint","IMPRINT",FACE,{"disambiguationData":[TD([[makeQuery(id+"F0.imprint","IMPRINT",EDGE,{"disambiguationData":[TD([[subQ2,-1.0]])],"derivedFrom":subQ1}),-1.0]])]});}
            var Q59;
            {var subQ0=sQuery(id+"F0.wireOp",EDGE,"E55");var subQ1=sQuery(id+"F0.wireOp",EDGE,"E0.right");var subQ2=makeQuery(id+"F0.imprint","INTERSECT",VERTEX,{"derivedFrom":[subQ1,subQ0]});Q59=makeQuery(id+"F0.imprint","IMPRINT",FACE,{"disambiguationData":[TD([[makeQuery(id+"F0.imprint","IMPRINT",EDGE,{"disambiguationData":[TD([[subQ2,-1.0]])],"derivedFrom":subQ1}),-1.0]])]});}
            var Q60;
            {var subQ6=sQuery(id+"F0.wireOp",EDGE,"E3.filletArc");Q60=makeQuery(id+"F0.imprint","IMPRINT",FACE,{"disambiguationData":[TD([[makeQuery(id+"F0.imprint","IMPRINT",EDGE,{"derivedFrom":subQ6}),1.0]])]});}
            var Q61;
            {var subQ0=sQuery(id+"F0.wireOp",EDGE,"E137");var subQ1=sQuery(id+"F0.wireOp",EDGE,"E1.right");var subQ2=makeQuery(id+"F0.imprint","INTERSECT",VERTEX,{"derivedFrom":[subQ1,subQ0]});Q61=makeQuery(id+"F0.imprint","IMPRINT",FACE,{"disambiguationData":[TD([[makeQuery(id+"F0.imprint","IMPRINT",EDGE,{"disambiguationData":[TD([[subQ2,-1.0]])],"derivedFrom":subQ1}),-1.0]])]});}
            var Q62;
            {var subQ0=sQuery(id+"F0.wireOp",EDGE,"E111");var subQ1=sQuery(id+"F0.wireOp",EDGE,"E1.bottom");var subQ2=makeQuery(id+"F0.imprint","INTERSECT",VERTEX,{"derivedFrom":[subQ1,subQ0]});Q62=makeQuery(id+"F0.imprint","IMPRINT",FACE,{"disambiguationData":[TD([[makeQuery(id+"F0.imprint","IMPRINT",EDGE,{"disambiguationData":[TD([[subQ2,-1.0]])],"derivedFrom":subQ1}),-1.0]])]});}
            var Q63;
            Q63=makeQuery(id+"F0.imprint","IMPRINT",FACE,{"disambiguationData":[TD([[makeQuery(id+"F0.imprint","IMPRINT",EDGE,{"derivedFrom":sQuery(id+"F0.wireOp",EDGE,"E149")}),1.0]])]});
            var Q64;
            Q64=makeQuery(id+"F0.imprint","IMPRINT",FACE,{"disambiguationData":[TD([[makeQuery(id+"F0.imprint","IMPRINT",EDGE,{"derivedFrom":sQuery(id+"F0.wireOp",EDGE,"CKmbeHNM-Plrr-UWmO-MxFq-oQQ4A1Si6NXd")}),1.0]])]});
            var Q65;
            Q65=makeQuery(id+"F0.imprint","IMPRINT",FACE,{"disambiguationData":[TD([[makeQuery(id+"F0.imprint","IMPRINT",EDGE,{"derivedFrom":sQuery(id+"F0.wireOp",EDGE,"E150")}),1.0]])]});
            var Q66;
            Q66=makeQuery(id+"F0.imprint","IMPRINT",FACE,{"disambiguationData":[TD([[makeQuery(id+"F0.imprint","IMPRINT",EDGE,{"derivedFrom":sQuery(id+"F0.wireOp",EDGE,"8quo0T1A-5u05-Fd0u-cEtL-LYPx0S1iHhuR")}),1.0]])]});
            var Q67;
            Q67=makeQuery(id+"F0.imprint","IMPRINT",FACE,{"disambiguationData":[TD([[makeQuery(id+"F0.imprint","IMPRINT",EDGE,{"derivedFrom":sQuery(id+"F0.wireOp",EDGE,"vzxEWEUf-tj6Q-O0Fc-aXnH-EtOi30AOdIHU")}),1.0]])]});
            var Q68;
            Q68=makeQuery(id+"F0.imprint","IMPRINT",FACE,{"disambiguationData":[TD([[makeQuery(id+"F0.imprint","IMPRINT",EDGE,{"derivedFrom":sQuery(id+"F0.wireOp",EDGE,"E151")}),1.0]])]});
            var Q69;
            Q69=makeQuery(id+"F0.imprint","IMPRINT",FACE,{"disambiguationData":[TD([[makeQuery(id+"F0.imprint","IMPRINT",EDGE,{"derivedFrom":sQuery(id+"F0.wireOp",EDGE,"g010j2id-ZlEN-OTWz-aQFt-1MfugEjwWQE0")}),1.0]])]});
            var Q70;
            Q70=makeQuery(id+"F0.imprint","IMPRINT",FACE,{"disambiguationData":[TD([[makeQuery(id+"F0.imprint","IMPRINT",EDGE,{"derivedFrom":sQuery(id+"F0.wireOp",EDGE,"E152")}),1.0]])]});
            var Q71;
            {var subQ0=sQuery(id+"F0.wireOp",EDGE,"E159");var subQ1=sQuery(id+"F0.wireOp",EDGE,"E10.filletArc");var subQ2=makeQuery(id+"F0.imprint","INTERSECT",VERTEX,{"disambiguationData":[OD(0.0)],"derivedFrom":[subQ1,subQ0]});Q71=makeQuery(id+"F0.imprint","IMPRINT",FACE,{"disambiguationData":[TD([[makeQuery(id+"F0.imprint","IMPRINT",EDGE,{"disambiguationData":[TD([[subQ2,-1.0]])],"derivedFrom":subQ1}),1.0]])]});}
            var Q72;
            {var subQ0=sQuery(id+"F0.wireOp",EDGE,"E160");var subQ1=sQuery(id+"F0.wireOp",EDGE,"E7.filletArc");var subQ2=makeQuery(id+"F0.imprint","INTERSECT",VERTEX,{"disambiguationData":[OD(0.0)],"derivedFrom":[subQ1,subQ0]});Q72=makeQuery(id+"F0.imprint","IMPRINT",FACE,{"disambiguationData":[TD([[makeQuery(id+"F0.imprint","IMPRINT",EDGE,{"disambiguationData":[TD([[subQ2,-1.0]])],"derivedFrom":subQ1}),1.0]])]});}
            var Q73;
            {var subQ0=sQuery(id+"F0.wireOp",EDGE,"E160");var subQ1=sQuery(id+"F0.wireOp",EDGE,"E7.filletArc");var subQ2=makeQuery(id+"F0.imprint","INTERSECT",VERTEX,{"disambiguationData":[OD(0.0)],"derivedFrom":[subQ1,subQ0]});Q73=makeQuery(id+"F0.imprint","IMPRINT",FACE,{"disambiguationData":[TD([[makeQuery(id+"F0.imprint","IMPRINT",EDGE,{"disambiguationData":[TD([[subQ2,-1.0]])],"derivedFrom":subQ1}),-1.0]])]});}
            var Q74;
            {var subQ0=sQuery(id+"F0.wireOp",EDGE,"E159");var subQ1=sQuery(id+"F0.wireOp",EDGE,"E10.filletArc");var subQ2=makeQuery(id+"F0.imprint","INTERSECT",VERTEX,{"disambiguationData":[OD(0.0)],"derivedFrom":[subQ1,subQ0]});Q74=makeQuery(id+"F0.imprint","IMPRINT",FACE,{"disambiguationData":[TD([[makeQuery(id+"F0.imprint","IMPRINT",EDGE,{"disambiguationData":[TD([[subQ2,-1.0]])],"derivedFrom":subQ1}),-1.0]])]});}
            var Q75;
            {var subQ0=sQuery(id+"F0.wireOp",EDGE,"E156");var subQ1=sQuery(id+"F0.wireOp",EDGE,"E8.filletArc");var subQ2=makeQuery(id+"F0.imprint","INTERSECT",VERTEX,{"disambiguationData":[OD(0.0)],"derivedFrom":[subQ1,subQ0]});Q75=makeQuery(id+"F0.imprint","IMPRINT",FACE,{"disambiguationData":[TD([[makeQuery(id+"F0.imprint","IMPRINT",EDGE,{"disambiguationData":[TD([[subQ2,-1.0]])],"derivedFrom":subQ1}),-1.0]])]});}
            var Q76;
            {var subQ0=sQuery(id+"F0.wireOp",EDGE,"E156");var subQ1=sQuery(id+"F0.wireOp",EDGE,"E8.filletArc");var subQ2=makeQuery(id+"F0.imprint","INTERSECT",VERTEX,{"disambiguationData":[OD(0.0)],"derivedFrom":[subQ1,subQ0]});Q76=makeQuery(id+"F0.imprint","IMPRINT",FACE,{"disambiguationData":[TD([[makeQuery(id+"F0.imprint","IMPRINT",EDGE,{"disambiguationData":[TD([[subQ2,-1.0]])],"derivedFrom":subQ1}),1.0]])]});}
            var Q77;
            {var subQ0=sQuery(id+"F0.wireOp",EDGE,"E155");var subQ1=sQuery(id+"F0.wireOp",EDGE,"E9.filletArc");var subQ2=makeQuery(id+"F0.imprint","INTERSECT",VERTEX,{"disambiguationData":[OD(0.0)],"derivedFrom":[subQ1,subQ0]});Q77=makeQuery(id+"F0.imprint","IMPRINT",FACE,{"disambiguationData":[TD([[makeQuery(id+"F0.imprint","IMPRINT",EDGE,{"disambiguationData":[TD([[subQ2,-1.0]])],"derivedFrom":subQ1}),1.0]])]});}
            var Q78;
            {var subQ0=sQuery(id+"F0.wireOp",EDGE,"E155");var subQ1=sQuery(id+"F0.wireOp",EDGE,"E9.filletArc");var subQ2=makeQuery(id+"F0.imprint","INTERSECT",VERTEX,{"disambiguationData":[OD(0.0)],"derivedFrom":[subQ1,subQ0]});Q78=makeQuery(id+"F0.imprint","IMPRINT",FACE,{"disambiguationData":[TD([[makeQuery(id+"F0.imprint","IMPRINT",EDGE,{"disambiguationData":[TD([[subQ2,-1.0]])],"derivedFrom":subQ1}),-1.0]])]});}
            extrude(context, id + "F1", {"entities" : qUnion([Q0, Q1, Q2, Q3, Q4, Q5, Q6, Q7, Q8, Q9, Q10, Q11, Q12, Q13, Q14, Q15, Q16, Q17, Q18, Q19, Q20, Q21, Q22, Q23, Q24, Q25, Q26, Q27, Q28, Q29, Q30, Q31, Q32, Q33, Q34, Q35, Q36, Q37, Q38, Q39, Q40, Q41, Q42, Q43, Q44, Q45, Q46, Q47, Q48, Q49, Q50, Q51, Q52, Q53, Q54, Q55, Q56, Q57, Q58, Q59, Q60, Q61, Q62, Q63, Q64, Q65, Q66, Q67, Q68, Q69, Q70, Q71, Q72, Q73, Q74, Q75, Q76, Q77, Q78]), "depth" : 6.35 * mm, "offsetDistance" : 25.4 * mm});
        }
        {
            var Q0;
            {var subQ0=sQuery(id+"F0.wireOp",EDGE,"E28");var subQ1=makeQuery(id+"F0.imprint","INTERSECT",VERTEX,{"derivedFrom":[sQuery(id+"F0.wireOp",EDGE,"E15.bottom"),subQ0]});Q0=makeQuery(id+"F0.imprint","IMPRINT",FACE,{"disambiguationData":[TD([[makeQuery(id+"F0.imprint","IMPRINT",EDGE,{"disambiguationData":[TD([[subQ1,-1.0]])],"derivedFrom":subQ0}),1.0]])]});}
            var Q1;
            {var subQ0=sQuery(id+"F0.wireOp",EDGE,"E30");var subQ1=makeQuery(id+"F0.imprint","INTERSECT",VERTEX,{"derivedFrom":[sQuery(id+"F0.wireOp",EDGE,"E15.bottom"),subQ0]});Q1=makeQuery(id+"F0.imprint","IMPRINT",FACE,{"disambiguationData":[TD([[makeQuery(id+"F0.imprint","IMPRINT",EDGE,{"disambiguationData":[TD([[subQ1,1.0]])],"derivedFrom":subQ0}),1.0]])]});}
            var Q2;
            Q2=makeQuery(id+"F0.imprint","IMPRINT",FACE,{"disambiguationData":[TD([[makeQuery(id+"F0.imprint","IMPRINT",EDGE,{"derivedFrom":sQuery(id+"F0.wireOp",EDGE,"E29")}),1.0]])]});
            var Q3;
            {var subQ0=sQuery(id+"F0.wireOp",EDGE,"E31");var subQ1=makeQuery(id+"F0.imprint","INTERSECT",VERTEX,{"derivedFrom":[sQuery(id+"F0.wireOp",EDGE,"E15.top"),subQ0]});Q3=makeQuery(id+"F0.imprint","IMPRINT",FACE,{"disambiguationData":[TD([[makeQuery(id+"F0.imprint","IMPRINT",EDGE,{"disambiguationData":[TD([[subQ1,1.0]])],"derivedFrom":subQ0}),1.0]])]});}
            var Q4;
            {var subQ0=sQuery(id+"F0.wireOp",EDGE,"E32");var subQ1=makeQuery(id+"F0.imprint","INTERSECT",VERTEX,{"derivedFrom":[sQuery(id+"F0.wireOp",EDGE,"E15.top"),subQ0]});Q4=makeQuery(id+"F0.imprint","IMPRINT",FACE,{"disambiguationData":[TD([[makeQuery(id+"F0.imprint","IMPRINT",EDGE,{"disambiguationData":[TD([[subQ1,1.0]])],"derivedFrom":subQ0}),1.0]])]});}
            extrude(context, id + "F2", {"entities" : qUnion([Q0, Q1, Q2, Q3, Q4]), "operationType" : NewBodyOperationType.ADD, "depth" : 12.7 * mm, "offsetDistance" : 25.4 * mm});
        }
        {
            var Q0;
            {var subQ0=sQuery(id+"F0.wireOp",EDGE,"E3.filletArc");Q0=makeQuery(id+"F0.imprint","IMPRINT",FACE,{"disambiguationData":[TD([[makeQuery(id+"F0.imprint","IMPRINT",EDGE,{"derivedFrom":subQ0}),-1.0]])]});}
            var Q1;
            {var subQ6=sQuery(id+"F0.wireOp",EDGE,"E3.filletArc");Q1=makeQuery(id+"F0.imprint","IMPRINT",FACE,{"disambiguationData":[TD([[makeQuery(id+"F0.imprint","IMPRINT",EDGE,{"derivedFrom":subQ6}),1.0]])]});}
            var Q2;
            {var subQ0=sQuery(id+"F0.wireOp",EDGE,"E53");var subQ1=sQuery(id+"F0.wireOp",EDGE,"E0.bottom");var subQ2=makeQuery(id+"F0.imprint","INTERSECT",VERTEX,{"derivedFrom":[subQ1,subQ0]});Q2=makeQuery(id+"F0.imprint","IMPRINT",FACE,{"disambiguationData":[TD([[makeQuery(id+"F0.imprint","IMPRINT",EDGE,{"disambiguationData":[TD([[subQ2,1.0]])],"derivedFrom":subQ1}),-1.0]])]});}
            var Q3;
            {var subQ0=sQuery(id+"F0.wireOp",EDGE,"E110");var subQ1=sQuery(id+"F0.wireOp",EDGE,"E1.bottom");var subQ2=makeQuery(id+"F0.imprint","INTERSECT",VERTEX,{"derivedFrom":[subQ1,subQ0]});Q3=makeQuery(id+"F0.imprint","IMPRINT",FACE,{"disambiguationData":[TD([[makeQuery(id+"F0.imprint","IMPRINT",EDGE,{"disambiguationData":[TD([[subQ2,-1.0]])],"derivedFrom":subQ1}),-1.0]])]});}
            var Q4;
            {var subQ0=sQuery(id+"F0.wireOp",EDGE,"E10.filletArc");Q4=makeQuery(id+"F0.imprint","IMPRINT",FACE,{"disambiguationData":[TD([[makeQuery(id+"F0.imprint","IMPRINT",EDGE,{"derivedFrom":subQ0}),1.0]])]});}
            var Q5;
            {var subQ0=sQuery(id+"F0.wireOp",EDGE,"E54");var subQ1=sQuery(id+"F0.wireOp",EDGE,"E0.bottom");var subQ2=makeQuery(id+"F0.imprint","INTERSECT",VERTEX,{"derivedFrom":[subQ1,subQ0]});Q5=makeQuery(id+"F0.imprint","IMPRINT",FACE,{"disambiguationData":[TD([[makeQuery(id+"F0.imprint","IMPRINT",EDGE,{"disambiguationData":[TD([[subQ2,-1.0]])],"derivedFrom":subQ1}),-1.0]])]});}
            var Q6;
            {var subQ0=sQuery(id+"F0.wireOp",EDGE,"E54");var subQ1=sQuery(id+"F0.wireOp",EDGE,"E1.bottom");var subQ2=makeQuery(id+"F0.imprint","INTERSECT",VERTEX,{"derivedFrom":[subQ1,subQ0]});Q6=makeQuery(id+"F0.imprint","IMPRINT",FACE,{"disambiguationData":[TD([[makeQuery(id+"F0.imprint","IMPRINT",EDGE,{"disambiguationData":[TD([[subQ2,-1.0]])],"derivedFrom":subQ1}),-1.0]])]});}
            var Q7;
            {var subQ0=sQuery(id+"F0.wireOp",EDGE,"E4.filletArc");Q7=makeQuery(id+"F0.imprint","IMPRINT",FACE,{"disambiguationData":[TD([[makeQuery(id+"F0.imprint","IMPRINT",EDGE,{"derivedFrom":subQ0}),-1.0]])]});}
            var Q8;
            {var subQ8=sQuery(id+"F0.wireOp",EDGE,"E4.filletArc");Q8=makeQuery(id+"F0.imprint","IMPRINT",FACE,{"disambiguationData":[TD([[makeQuery(id+"F0.imprint","IMPRINT",EDGE,{"derivedFrom":subQ8}),1.0]])]});}
            var Q9;
            {var subQ0=sQuery(id+"F0.wireOp",EDGE,"E7.filletArc");Q9=makeQuery(id+"F0.imprint","IMPRINT",FACE,{"disambiguationData":[TD([[makeQuery(id+"F0.imprint","IMPRINT",EDGE,{"derivedFrom":subQ0}),1.0]])]});}
            var Q10;
            {var subQ0=sQuery(id+"F0.wireOp",EDGE,"E60");var subQ1=sQuery(id+"F0.wireOp",EDGE,"E0.left");var subQ2=makeQuery(id+"F0.imprint","INTERSECT",VERTEX,{"derivedFrom":[subQ1,subQ0]});Q10=makeQuery(id+"F0.imprint","IMPRINT",FACE,{"disambiguationData":[TD([[makeQuery(id+"F0.imprint","IMPRINT",EDGE,{"disambiguationData":[TD([[subQ2,1.0]])],"derivedFrom":subQ1}),1.0]])]});}
            var Q11;
            {var subQ0=sQuery(id+"F0.wireOp",EDGE,"E134");var subQ1=sQuery(id+"F0.wireOp",EDGE,"E1.left");var subQ2=makeQuery(id+"F0.imprint","INTERSECT",VERTEX,{"derivedFrom":[subQ1,subQ0]});Q11=makeQuery(id+"F0.imprint","IMPRINT",FACE,{"disambiguationData":[TD([[makeQuery(id+"F0.imprint","IMPRINT",EDGE,{"disambiguationData":[TD([[subQ2,-1.0]])],"derivedFrom":subQ1}),1.0]])]});}
            var Q12;
            {var subQ0=sQuery(id+"F0.wireOp",EDGE,"E136");var subQ1=sQuery(id+"F0.wireOp",EDGE,"E1.right");var subQ2=makeQuery(id+"F0.imprint","INTERSECT",VERTEX,{"derivedFrom":[subQ1,subQ0]});Q12=makeQuery(id+"F0.imprint","IMPRINT",FACE,{"disambiguationData":[TD([[makeQuery(id+"F0.imprint","IMPRINT",EDGE,{"disambiguationData":[TD([[subQ2,-1.0]])],"derivedFrom":subQ1}),-1.0]])]});}
            var Q13;
            {var subQ0=sQuery(id+"F0.wireOp",EDGE,"E55");var subQ1=sQuery(id+"F0.wireOp",EDGE,"E0.right");var subQ2=makeQuery(id+"F0.imprint","INTERSECT",VERTEX,{"derivedFrom":[subQ1,subQ0]});Q13=makeQuery(id+"F0.imprint","IMPRINT",FACE,{"disambiguationData":[TD([[makeQuery(id+"F0.imprint","IMPRINT",EDGE,{"disambiguationData":[TD([[subQ2,1.0]])],"derivedFrom":subQ1}),-1.0]])]});}
            var Q14;
            {var subQ0=sQuery(id+"F0.wireOp",EDGE,"E56");var subQ1=sQuery(id+"F0.wireOp",EDGE,"E0.right");var subQ2=makeQuery(id+"F0.imprint","INTERSECT",VERTEX,{"derivedFrom":[subQ1,subQ0]});Q14=makeQuery(id+"F0.imprint","IMPRINT",FACE,{"disambiguationData":[TD([[makeQuery(id+"F0.imprint","IMPRINT",EDGE,{"disambiguationData":[TD([[subQ2,-1.0]])],"derivedFrom":subQ1}),-1.0]])]});}
            var Q15;
            {var subQ0=sQuery(id+"F0.wireOp",EDGE,"E56");var subQ1=sQuery(id+"F0.wireOp",EDGE,"E1.right");var subQ2=makeQuery(id+"F0.imprint","INTERSECT",VERTEX,{"derivedFrom":[subQ1,subQ0]});Q15=makeQuery(id+"F0.imprint","IMPRINT",FACE,{"disambiguationData":[TD([[makeQuery(id+"F0.imprint","IMPRINT",EDGE,{"disambiguationData":[TD([[subQ2,-1.0]])],"derivedFrom":subQ1}),-1.0]])]});}
            var Q16;
            {var subQ0=sQuery(id+"F0.wireOp",EDGE,"E59");var subQ1=sQuery(id+"F0.wireOp",EDGE,"E1.left");var subQ2=makeQuery(id+"F0.imprint","INTERSECT",VERTEX,{"derivedFrom":[subQ1,subQ0]});Q16=makeQuery(id+"F0.imprint","IMPRINT",FACE,{"disambiguationData":[TD([[makeQuery(id+"F0.imprint","IMPRINT",EDGE,{"disambiguationData":[TD([[subQ2,-1.0]])],"derivedFrom":subQ1}),1.0]])]});}
            var Q17;
            {var subQ0=sQuery(id+"F0.wireOp",EDGE,"E59");var subQ1=sQuery(id+"F0.wireOp",EDGE,"E0.left");var subQ2=makeQuery(id+"F0.imprint","INTERSECT",VERTEX,{"derivedFrom":[subQ1,subQ0]});Q17=makeQuery(id+"F0.imprint","IMPRINT",FACE,{"disambiguationData":[TD([[makeQuery(id+"F0.imprint","IMPRINT",EDGE,{"disambiguationData":[TD([[subQ2,-1.0]])],"derivedFrom":subQ1}),1.0]])]});}
            var Q18;
            {var subQ0=sQuery(id+"F0.wireOp",EDGE,"E6.filletArc");Q18=makeQuery(id+"F0.imprint","IMPRINT",FACE,{"disambiguationData":[TD([[makeQuery(id+"F0.imprint","IMPRINT",EDGE,{"derivedFrom":subQ0}),-1.0]])]});}
            var Q19;
            {var subQ5=sQuery(id+"F0.wireOp",EDGE,"E6.filletArc");Q19=makeQuery(id+"F0.imprint","IMPRINT",FACE,{"disambiguationData":[TD([[makeQuery(id+"F0.imprint","IMPRINT",EDGE,{"derivedFrom":subQ5}),1.0]])]});}
            var Q20;
            {var subQ0=sQuery(id+"F0.wireOp",EDGE,"E9.filletArc");Q20=makeQuery(id+"F0.imprint","IMPRINT",FACE,{"disambiguationData":[TD([[makeQuery(id+"F0.imprint","IMPRINT",EDGE,{"derivedFrom":subQ0}),1.0]])]});}
            var Q21;
            {var subQ0=sQuery(id+"F0.wireOp",EDGE,"E8.filletArc");Q21=makeQuery(id+"F0.imprint","IMPRINT",FACE,{"disambiguationData":[TD([[makeQuery(id+"F0.imprint","IMPRINT",EDGE,{"derivedFrom":subQ0}),1.0]])]});}
            var Q22;
            {var subQ6=sQuery(id+"F0.wireOp",EDGE,"E5.filletArc");Q22=makeQuery(id+"F0.imprint","IMPRINT",FACE,{"disambiguationData":[TD([[makeQuery(id+"F0.imprint","IMPRINT",EDGE,{"derivedFrom":subQ6}),1.0]])]});}
            var Q23;
            {var subQ0=sQuery(id+"F0.wireOp",EDGE,"E5.filletArc");Q23=makeQuery(id+"F0.imprint","IMPRINT",FACE,{"disambiguationData":[TD([[makeQuery(id+"F0.imprint","IMPRINT",EDGE,{"derivedFrom":subQ0}),-1.0]])]});}
            var Q24;
            {var subQ0=sQuery(id+"F0.wireOp",EDGE,"E57");var subQ1=sQuery(id+"F0.wireOp",EDGE,"E1.top");var subQ2=makeQuery(id+"F0.imprint","INTERSECT",VERTEX,{"derivedFrom":[subQ1,subQ0]});Q24=makeQuery(id+"F0.imprint","IMPRINT",FACE,{"disambiguationData":[TD([[makeQuery(id+"F0.imprint","IMPRINT",EDGE,{"disambiguationData":[TD([[subQ2,-1.0]])],"derivedFrom":subQ1}),1.0]])]});}
            var Q25;
            {var subQ0=sQuery(id+"F0.wireOp",EDGE,"E57");var subQ1=sQuery(id+"F0.wireOp",EDGE,"E0.top");var subQ2=makeQuery(id+"F0.imprint","INTERSECT",VERTEX,{"derivedFrom":[subQ1,subQ0]});Q25=makeQuery(id+"F0.imprint","IMPRINT",FACE,{"disambiguationData":[TD([[makeQuery(id+"F0.imprint","IMPRINT",EDGE,{"disambiguationData":[TD([[subQ2,-1.0]])],"derivedFrom":subQ1}),1.0]])]});}
            var Q26;
            {var subQ0=sQuery(id+"F0.wireOp",EDGE,"E58");var subQ1=sQuery(id+"F0.wireOp",EDGE,"E0.top");var subQ2=makeQuery(id+"F0.imprint","INTERSECT",VERTEX,{"derivedFrom":[subQ1,subQ0]});Q26=makeQuery(id+"F0.imprint","IMPRINT",FACE,{"disambiguationData":[TD([[makeQuery(id+"F0.imprint","IMPRINT",EDGE,{"disambiguationData":[TD([[subQ2,1.0]])],"derivedFrom":subQ1}),1.0]])]});}
            var Q27;
            {var subQ0=sQuery(id+"F0.wireOp",EDGE,"E115");var subQ1=sQuery(id+"F0.wireOp",EDGE,"E1.top");var subQ2=makeQuery(id+"F0.imprint","INTERSECT",VERTEX,{"derivedFrom":[subQ1,subQ0]});Q27=makeQuery(id+"F0.imprint","IMPRINT",FACE,{"disambiguationData":[TD([[makeQuery(id+"F0.imprint","IMPRINT",EDGE,{"disambiguationData":[TD([[subQ2,-1.0]])],"derivedFrom":subQ1}),1.0]])]});}
            extrude(context, id + "F3", {"entities" : qUnion([Q0, Q1, Q2, Q3, Q4, Q5, Q6, Q7, Q8, Q9, Q10, Q11, Q12, Q13, Q14, Q15, Q16, Q17, Q18, Q19, Q20, Q21, Q22, Q23, Q24, Q25, Q26, Q27]), "operationType" : NewBodyOperationType.ADD, "depth" : 31.75 * mm, "offsetDistance" : 25.4 * mm});
        }
        {
            var Q0;
            {var subQ0=sQuery(id+"F0.wireOp",EDGE,"E53");var subQ1=sQuery(id+"F0.wireOp",EDGE,"E0.bottom");var subQ2=makeQuery(id+"F0.imprint","INTERSECT",VERTEX,{"derivedFrom":[subQ1,subQ0]});Q0=makeQuery(id+"F0.imprint","IMPRINT",FACE,{"disambiguationData":[TD([[makeQuery(id+"F0.imprint","IMPRINT",EDGE,{"disambiguationData":[TD([[subQ2,-1.0]])],"derivedFrom":subQ1}),-1.0]])]});}
            var Q1;
            {var subQ0=sQuery(id+"F0.wireOp",EDGE,"E53");var subQ1=sQuery(id+"F0.wireOp",EDGE,"E1.bottom");var subQ2=makeQuery(id+"F0.imprint","INTERSECT",VERTEX,{"derivedFrom":[subQ1,subQ0]});Q1=makeQuery(id+"F0.imprint","IMPRINT",FACE,{"disambiguationData":[TD([[makeQuery(id+"F0.imprint","IMPRINT",EDGE,{"disambiguationData":[TD([[subQ2,-1.0]])],"derivedFrom":subQ1}),-1.0]])]});}
            var Q2;
            {var subQ0=sQuery(id+"F0.wireOp",EDGE,"E55");var subQ1=sQuery(id+"F0.wireOp",EDGE,"E1.right");var subQ2=makeQuery(id+"F0.imprint","INTERSECT",VERTEX,{"derivedFrom":[subQ1,subQ0]});Q2=makeQuery(id+"F0.imprint","IMPRINT",FACE,{"disambiguationData":[TD([[makeQuery(id+"F0.imprint","IMPRINT",EDGE,{"disambiguationData":[TD([[subQ2,-1.0]])],"derivedFrom":subQ1}),-1.0]])]});}
            var Q3;
            {var subQ0=sQuery(id+"F0.wireOp",EDGE,"E55");var subQ1=sQuery(id+"F0.wireOp",EDGE,"E0.right");var subQ2=makeQuery(id+"F0.imprint","INTERSECT",VERTEX,{"derivedFrom":[subQ1,subQ0]});Q3=makeQuery(id+"F0.imprint","IMPRINT",FACE,{"disambiguationData":[TD([[makeQuery(id+"F0.imprint","IMPRINT",EDGE,{"disambiguationData":[TD([[subQ2,-1.0]])],"derivedFrom":subQ1}),-1.0]])]});}
            var Q4;
            {var subQ0=sQuery(id+"F0.wireOp",EDGE,"E60");var subQ1=sQuery(id+"F0.wireOp",EDGE,"E1.left");var subQ2=makeQuery(id+"F0.imprint","INTERSECT",VERTEX,{"derivedFrom":[subQ1,subQ0]});Q4=makeQuery(id+"F0.imprint","IMPRINT",FACE,{"disambiguationData":[TD([[makeQuery(id+"F0.imprint","IMPRINT",EDGE,{"disambiguationData":[TD([[subQ2,-1.0]])],"derivedFrom":subQ1}),1.0]])]});}
            var Q5;
            {var subQ0=sQuery(id+"F0.wireOp",EDGE,"E59");var subQ1=sQuery(id+"F0.wireOp",EDGE,"E0.left");var subQ2=makeQuery(id+"F0.imprint","INTERSECT",VERTEX,{"derivedFrom":[subQ1,subQ0]});Q5=makeQuery(id+"F0.imprint","IMPRINT",FACE,{"disambiguationData":[TD([[makeQuery(id+"F0.imprint","IMPRINT",EDGE,{"disambiguationData":[TD([[subQ2,1.0]])],"derivedFrom":subQ1}),1.0]])]});}
            var Q6;
            {var subQ0=sQuery(id+"F0.wireOp",EDGE,"E57");var subQ1=sQuery(id+"F0.wireOp",EDGE,"E0.top");var subQ2=makeQuery(id+"F0.imprint","INTERSECT",VERTEX,{"derivedFrom":[subQ1,subQ0]});Q6=makeQuery(id+"F0.imprint","IMPRINT",FACE,{"disambiguationData":[TD([[makeQuery(id+"F0.imprint","IMPRINT",EDGE,{"disambiguationData":[TD([[subQ2,1.0]])],"derivedFrom":subQ1}),1.0]])]});}
            var Q7;
            {var subQ0=sQuery(id+"F0.wireOp",EDGE,"E58");var subQ1=sQuery(id+"F0.wireOp",EDGE,"E1.top");var subQ2=makeQuery(id+"F0.imprint","INTERSECT",VERTEX,{"derivedFrom":[subQ1,subQ0]});Q7=makeQuery(id+"F0.imprint","IMPRINT",FACE,{"disambiguationData":[TD([[makeQuery(id+"F0.imprint","IMPRINT",EDGE,{"disambiguationData":[TD([[subQ2,-1.0]])],"derivedFrom":subQ1}),1.0]])]});}
            extrude(context, id + "F4", {"entities" : qUnion([Q0, Q1, Q2, Q3, Q4, Q5, Q6, Q7]), "operationType" : NewBodyOperationType.ADD, "depth" : 25.4 * mm, "offsetDistance" : 25.4 * mm});
        }
    });
